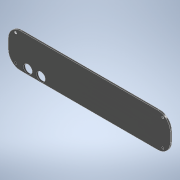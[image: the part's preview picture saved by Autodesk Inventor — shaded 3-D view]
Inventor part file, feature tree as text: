
AUTODESK INVENTOR PART (.ipt)
format: ipt  version: 2021 (Build 250183000, 183)  size: 163,328 bytes
history: native  units: mm
features: other x3, extrude x1, sketch x1
ambient origin geometry x8: Origin, YZ Plane, XZ Plane, XY Plane, X Axis, Y Axis, Z Axis, Center Point
bodies: Solid1 (feature_tree)
feature tree (5):
  other  "7 Segment Clock 3mm Walls.ipt"
  extrude  "Extrusion1"  TaperAngle=0.0deg  [1 undecoded]
  other  "FrontCover::7 Segment Clock 3mm Walls.ipt"
  other  "TaggingFeature1"
  sketch  "Sketch1"  dims[d0=10.0mm d1=0.0mm d2=0.0mm d3=0.0mm d4=0.0mm d5=0.0mm d6=0.0mm d7=0.0mm d8=0.0mm d9=0.0mm d10=0.0mm d11=0.0mm d12=0.0mm d13=0.0mm d14=0.0mm d15=0.0mm d16=0.0mm d17=0.0mm d18=0.0mm d19=0.0mm d20=0.0mm d21=0.0mm d22=2.0mm d23=0.0mm]
note: 1 required parameter value undecoded (feature->parameter linkage not recoverable at this tier; creation-order binding heuristic only, values carry confidence <= 0.55)
